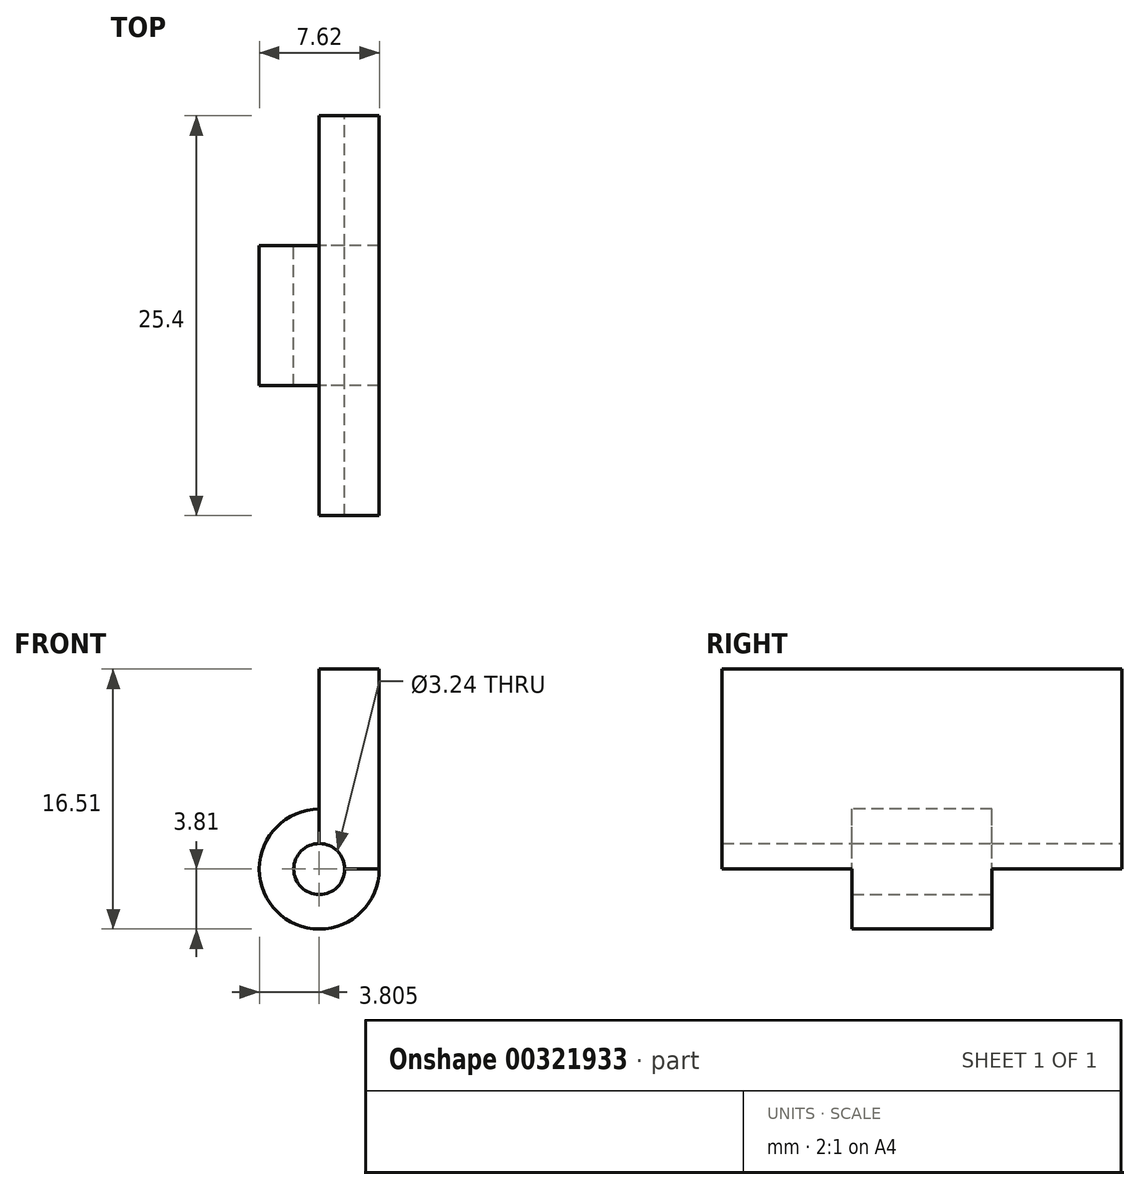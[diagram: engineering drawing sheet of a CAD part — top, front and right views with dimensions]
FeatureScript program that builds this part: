
annotation { "Feature Type Name" : "Feature", "Feature Type Description" : "" }
export const myFeature = defineFeature(function(context is Context, id is Id, definition is map)
    precondition{}
    {
        {
            var Q0;
            Q0=qCreatedBy(makeId("Front.planeOp"),FACE);
            var sketch = newSketch(context, id + "F0", { "sketchPlane" : qUnion([Q0])});
            skLineSegment(sketch, "E0.bottom", {"start": v(1.9, -6.35) * mm, "end": v(-1.9, -6.35) * mm});
            skLineSegment(sketch, "E0.top", {"start": v(1.9, 6.35) * mm, "end": v(-1.9, 6.35) * mm});
            skLineSegment(sketch, "E0.left", {"start": v(1.9, -6.35) * mm, "end": v(1.9, 6.35) * mm});
            skLineSegment(sketch, "E0.right", {"start": v(-1.9, -6.35) * mm, "end": v(-1.9, 6.35) * mm});
            skPoint(sketch, "E0.middle", {"position": v(0, 0) * mm});
            skSolve(sketch);
        }
        {
            var Q0;
            Q0 = qSketchRegion(id + "F0", true);
            extrude(context, id + "F1", {"entities" : qUnion([Q0]), "depth" : 12.7 * mm});
        }
        {
            var Q0;
            Q0=makeQuery(id+"F1.opExtrude","CAP_FACE",FACE,{"disambiguationData":[OSD([sQuery(id+"F0.wireOp",EDGE,"E0.bottom"),sQuery(id+"F0.wireOp",EDGE,"E0.top"),sQuery(id+"F0.wireOp",EDGE,"E0.left"),sQuery(id+"F0.wireOp",EDGE,"E0.right")])],"isStart":true});
            var sketch = newSketch(context, id + "F2", { "sketchPlane" : qUnion([Q0])});
            skArc(sketch, "E1", {"start": v(-1.9, -6.35) * mm, "mid": v(4.6, -9.04) * mm, "end": v(1.9, -2.54) * mm});
            skLineSegment(sketch, "E2", {"start": v(-1.9, -6.35) * mm, "end": v(1.9, -6.35) * mm});
            skLineSegment(sketch, "E3", {"start": v(1.9, -6.35) * mm, "end": v(1.9, -2.54) * mm});
            skSolve(sketch);
        }
        {
            var Q0;
            {var subQ1=makeQuery(id+"F1.opExtrude","CAP_EDGE",EDGE,{"disambiguationData":[OSD([sQuery(id+"F0.wireOp",EDGE,"E0.bottom")])],"isStart":true});Q0=makeQuery(id+"F2.imprint","IMPRINT",FACE,{"disambiguationData":[TD([[makeQuery(id+"F2.imprint","IMPRINT",EDGE,{"derivedFrom":subQ1}),1.0]])]});}
            var Q1;
            Q1=makeQuery(id+"F2.imprint","IMPRINT",FACE,{"disambiguationData":[TD([[makeQuery(id+"F2.imprint","IMPRINT",EDGE,{"derivedFrom":sQuery(id+"F2.wireOp",EDGE,"E1")}),1.0]])]});
            var Q2;
            Q2 = qConstructionFilter(qBodyType(qCreatedBy(id + "F2" ,EDGE), BodyType.WIRE), ConstructionObject.NO);
            extrude(context, id + "F3", {"entities" : qUnion([Q0, Q1]), "operationType" : NewBodyOperationType.ADD, "surfaceEntities" : qUnion([Q2]), "endBound" : BoundingType.SYMMETRIC, "depth" : 8.9 * mm});
        }
        {
            var Q0;
            Q0=makeQuery(id+"F1.opExtrude","CAP_FACE",FACE,{"disambiguationData":[OSD([sQuery(id+"F0.wireOp",EDGE,"E0.bottom"),sQuery(id+"F0.wireOp",EDGE,"E0.top"),sQuery(id+"F0.wireOp",EDGE,"E0.left"),sQuery(id+"F0.wireOp",EDGE,"E0.right")])],"isStart":true});
            var sketch = newSketch(context, id + "F4", { "sketchPlane" : qUnion([Q0])});
            skLineSegment(sketch, "E4.bottom", {"start": v(1.9, 6.35) * mm, "end": v(-1.9, 6.35) * mm});
            skLineSegment(sketch, "E4.top", {"start": v(1.9, -6.35) * mm, "end": v(-1.9, -6.35) * mm});
            skLineSegment(sketch, "E4.left", {"start": v(1.9, 6.35) * mm, "end": v(1.9, -6.35) * mm});
            skLineSegment(sketch, "E4.right", {"start": v(-1.9, 6.35) * mm, "end": v(-1.9, -6.35) * mm});
            skPoint(sketch, "E4.middle", {"position": v(0, 0) * mm});
            skSolve(sketch);
        }
        {
            var Q0;
            Q0 = qSketchRegion(id + "F4", true);
            extrude(context, id + "F5", {"entities" : qUnion([Q0]), "operationType" : NewBodyOperationType.ADD, "depth" : 12.7 * mm});
        }
        {
            var Q0;
            Q0=makeQuery(id+"F5.opExtrude","CAP_FACE",FACE,{"disambiguationData":[OSD([sQuery(id+"F4.wireOp",EDGE,"E4.bottom"),sQuery(id+"F4.wireOp",EDGE,"E4.top"),sQuery(id+"F4.wireOp",EDGE,"E4.left"),sQuery(id+"F4.wireOp",EDGE,"E4.right")])],"isStart":false});
            var sketch = newSketch(context, id + "F6", { "sketchPlane" : qUnion([Q0])});
            skCircle(sketch, "E5", {"center": v(1.9, -6.35) * mm, "radius": 1.62 * mm});
            skSolve(sketch);
        }
        {
            var Q0;
            Q0 = qSketchRegion(id + "F6", true);
            extrude(context, id + "F7", {"entities" : qUnion([Q0]), "operationType" : NewBodyOperationType.REMOVE, "oppositeDirection" : true, "depth" : 25.4 * mm});
        }
    });
